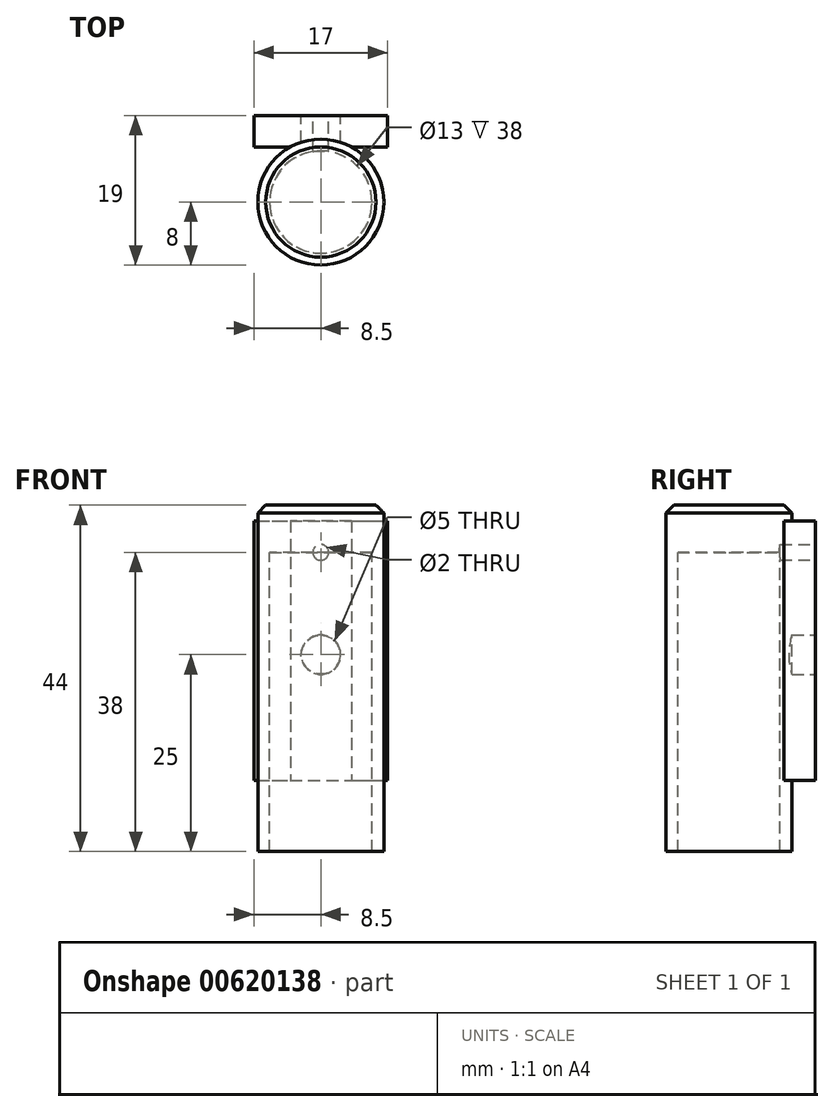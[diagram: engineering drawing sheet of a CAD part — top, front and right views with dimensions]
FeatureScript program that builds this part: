
annotation { "Feature Type Name" : "Feature", "Feature Type Description" : "" }
export const myFeature = defineFeature(function(context is Context, id is Id, definition is map)
    precondition{}
    {
        {
            var Q0;
            Q0=qCreatedBy(makeId("Front.planeOp"),FACE);
            var sketch = newSketch(context, id + "F0", { "sketchPlane" : qUnion([Q0])});
            skLineSegment(sketch, "E0.bottom", {"start": v(0, 0) * mm, "end": v(17, 0) * mm});
            skLineSegment(sketch, "E0.top", {"start": v(0, 33) * mm, "end": v(17, 33) * mm});
            skLineSegment(sketch, "E0.left", {"start": v(0, 0) * mm, "end": v(0, 33) * mm});
            skLineSegment(sketch, "E0.right", {"start": v(17, 0) * mm, "end": v(17, 33) * mm});
            skLineSegment(sketch, "E1", {"start": v(8.5, 33) * mm, "end": v(8.5, 0) * mm, "construction": true});
            skCircle(sketch, "E2", {"center": v(8.5, 16) * mm, "radius": 2.5 * mm});
            skCircle(sketch, "E3", {"center": v(8.5, 29) * mm, "radius": 1 * mm});
            skSolve(sketch);
        }
        {
            var Q0;
            Q0=makeQuery(id+"F0.imprint","IMPRINT",FACE,{"disambiguationData":[TD([[makeQuery(id+"F0.imprint","IMPRINT",EDGE,{"derivedFrom":sQuery(id+"F0.wireOp",EDGE,"E0.bottom")}),1.0]])]});
            extrude(context, id + "F1", {"entities" : qUnion([Q0]), "depth" : 4 * mm, "offsetDistance" : 25 * mm});
        }
        {
            var Q0;
            Q0=makeQuery(id+"F1.opExtrude","SWEPT_FACE",FACE,{"disambiguationData":[OSD([sQuery(id+"F0.wireOp",EDGE,"E0.bottom")])]});
            var sketch = newSketch(context, id + "F2", { "sketchPlane" : qUnion([Q0])});
            skLineSegment(sketch, "E4.0", {"start": v(0, 0) * mm, "end": v(17, 0) * mm});
            skLineSegment(sketch, "E5.0", {"start": v(0, 4) * mm, "end": v(0, 0) * mm});
            skLineSegment(sketch, "E6.0", {"start": v(17, 4) * mm, "end": v(17, 0) * mm});
            skLineSegment(sketch, "E7", {"start": v(0, 3) * mm, "end": v(8.5, 3) * mm});
            skPoint(sketch, "E8", {"position": v(8.5, 3) * mm});
            skLineSegment(sketch, "E9", {"start": v(0, 4) * mm, "end": v(17, 4) * mm});
            skArc(sketch, "E10", {"start": v(4.63, 4) * mm, "mid": v(8.5, 3) * mm, "end": v(12.37, 4) * mm});
            skArc(sketch, "E11", {"start": v(12.37, 4) * mm, "mid": v(8.5, 19) * mm, "end": v(4.63, 4) * mm, "construction": true});
            skLineSegment(sketch, "E12", {"start": v(8.5, 3) * mm, "end": v(17, 3) * mm});
            skSolve(sketch);
        }
        {
            var Q0;
            {var subQ0=sQuery(id+"F2.wireOp",EDGE,"E10");var subQ1=sQuery(id+"F2.wireOp",EDGE,"E9");var subQ2=makeQuery(id+"F2.imprint","INTERSECT",VERTEX,{"disambiguationData":[OD(0.0)],"derivedFrom":[subQ1,subQ0]});Q0=makeQuery(id+"F2.imprint","IMPRINT",FACE,{"disambiguationData":[TD([[makeQuery(id+"F2.imprint","IMPRINT",EDGE,{"disambiguationData":[TD([[subQ2,-1.0]])],"derivedFrom":subQ1}),-1.0]])]});}
            var Q1;
            Q1=makeQuery(id+"F1.opExtrude","SWEPT_FACE",FACE,{"disambiguationData":[OSD([sQuery(id+"F0.wireOp",EDGE,"E0.top")])]});
            extrude(context, id + "F3", {"entities" : qUnion([Q0]), "operationType" : NewBodyOperationType.REMOVE, "endBound" : BoundingType.UP_TO_SURFACE, "oppositeDirection" : true, "depth" : 25 * mm, "endBoundEntityFace" : qUnion([Q1]), "offsetDistance" : 25 * mm});
        }
        {
            var Q0;
            Q0=makeQuery(id+"F1.opExtrude","SWEPT_FACE",FACE,{"disambiguationData":[OSD([sQuery(id+"F0.wireOp",EDGE,"E0.top")])]});
            var sketch = newSketch(context, id + "F4", { "sketchPlane" : qUnion([Q0])});
            skArc(sketch, "E13.0", {"start": v(4.63, -4) * mm, "mid": v(8.5, -3) * mm, "end": v(12.37, -4) * mm});
            skCircle(sketch, "E14", {"center": v(8.5, -11) * mm, "radius": 8 * mm});
            skCircle(sketch, "E15", {"center": v(8.5, -11) * mm, "radius": 6.5 * mm});
            skSolve(sketch);
        }
        {
            var Q0;
            {var subQ0=sQuery(id+"F4.wireOp",EDGE,"E14");Q0=makeQuery(id+"F4.imprint","IMPRINT",FACE,{"disambiguationData":[TD([[makeQuery(id+"F4.imprint","IMPRINT",EDGE,{"disambiguationData":[OD(0.0)],"derivedFrom":subQ0}),1.0]])]});}
            extrude(context, id + "F5", {"entities" : qUnion([Q0]), "oppositeDirection" : true, "depth" : 42 * mm, "offsetDistance" : 25 * mm});
        }
        {
            var Q0;
            {var subQ0=sQuery(id+"F0.wireOp",EDGE,"E0.bottom");var subQ1=sQuery(id+"F0.wireOp",EDGE,"E0.right");var subQ2=sQuery(id+"F0.wireOp",EDGE,"E0.top");Q0=makeQuery(id+"F3.boolean.opBoolean","SPLIT",FACE,{"disambiguationData":[TD([makeQuery(id+"F1.opExtrude","SWEPT_FACE",FACE,{"disambiguationData":[OSD([subQ1])]})])],"derivedFrom":makeQuery(id+"F1.opExtrude","CAP_FACE",FACE,{"disambiguationData":[OSD([subQ0,subQ2,sQuery(id+"F0.wireOp",EDGE,"E0.left"),subQ1,sQuery(id+"F0.wireOp",EDGE,"E2"),sQuery(id+"F0.wireOp",EDGE,"E3")])],"isStart":false})});}
            var sketch = newSketch(context, id + "F6", { "sketchPlane" : qUnion([Q0])});
            skCircle(sketch, "E16.0", {"center": v(8.5, 29) * mm, "radius": 1 * mm});
            skSolve(sketch);
        }
        {
            var Q0;
            Q0=makeQuery(id+"F6.imprint","IMPRINT",FACE,{"disambiguationData":[TD([[makeQuery(id+"F6.imprint","IMPRINT",EDGE,{"derivedFrom":sQuery(id+"F6.wireOp",EDGE,"E16.0")}),1.0]])]});
            var Q1;
            Q1=makeQuery(id+"F5.opExtrude","SWEPT_FACE",FACE,{"disambiguationData":[OSD([sQuery(id+"F4.wireOp",EDGE,"E14")])]});
            extrude(context, id + "F7", {"entities" : qUnion([Q0]), "operationType" : NewBodyOperationType.REMOVE, "endBound" : BoundingType.SYMMETRIC, "depth" : 2 * mm, "endBoundEntityFace" : qUnion([Q1]), "offsetDistance" : 25 * mm});
        }
        {
            var Q0;
            Q0=makeQuery(id+"F5.opExtrude","CAP_FACE",FACE,{"disambiguationData":[OSD([sQuery(id+"F4.wireOp",EDGE,"E14"),sQuery(id+"F4.wireOp",EDGE,"E15")])],"isStart":true});
            var sketch = newSketch(context, id + "F8", { "sketchPlane" : qUnion([Q0])});
            skCircle(sketch, "E17.0", {"center": v(8.5, -11) * mm, "radius": 6.5 * mm});
            skCircle(sketch, "E18.0", {"center": v(8.5, -11) * mm, "radius": 8 * mm});
            skSolve(sketch);
        }
        {
            var Q0;
            Q0=makeQuery(id+"F8.imprint","IMPRINT",FACE,{"disambiguationData":[TD([[makeQuery(id+"F8.imprint","IMPRINT",EDGE,{"derivedFrom":sQuery(id+"F8.wireOp",EDGE,"E17.0")}),1.0]])]});
            extrude(context, id + "F9", {"entities" : qUnion([Q0]), "oppositeDirection" : true, "depth" : 4 * mm, "offsetDistance" : 25 * mm});
        }
        {
            var Q0;
            Q0=makeQuery(id+"F8.imprint","IMPRINT",FACE,{"disambiguationData":[TD([[makeQuery(id+"F8.imprint","IMPRINT",EDGE,{"derivedFrom":sQuery(id+"F8.wireOp",EDGE,"E17.0")}),-1.0]])]});
            var Q1;
            Q1=makeQuery(id+"F8.imprint","IMPRINT",FACE,{"disambiguationData":[TD([[makeQuery(id+"F8.imprint","IMPRINT",EDGE,{"derivedFrom":sQuery(id+"F8.wireOp",EDGE,"E17.0")}),1.0]])]});
            extrude(context, id + "F10", {"entities" : qUnion([Q0, Q1]), "operationType" : NewBodyOperationType.ADD, "depth" : 2 * mm, "offsetDistance" : 25 * mm});
        }
        {
            var Q0;
            Q0=makeQuery(id+"F10.opExtrude","CAP_EDGE",EDGE,{"disambiguationData":[OSD([sQuery(id+"F8.wireOp",EDGE,"E18.0")])],"isStart":false});
            chamfer(context, id + "F11", {"entities" : qUnion([Q0]), "width" : 1 * mm, "tangentPropagation" : true});
        }
    });
